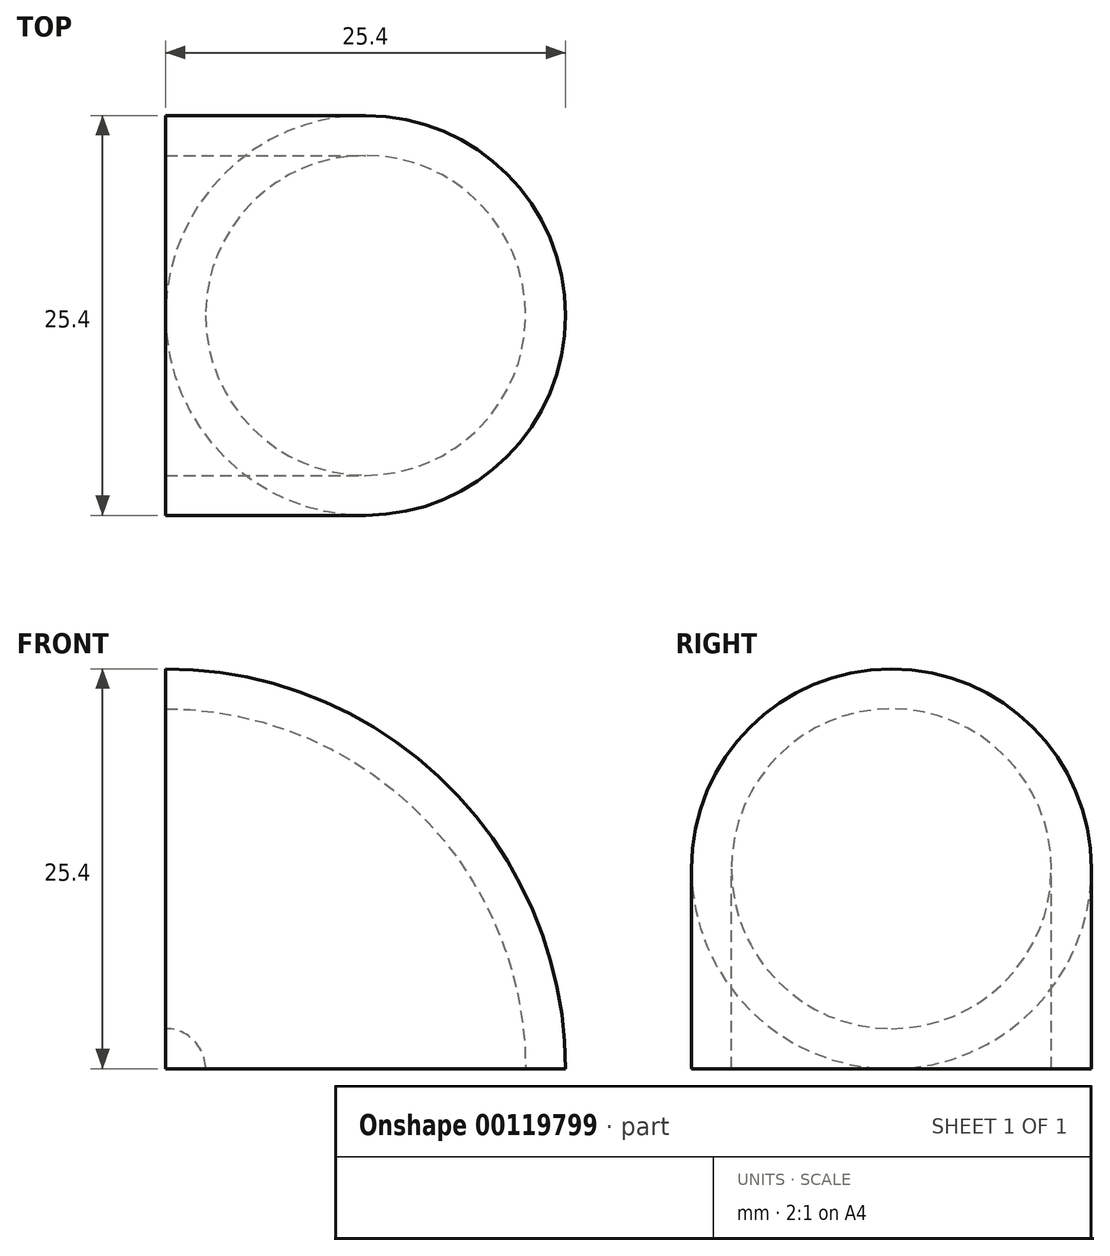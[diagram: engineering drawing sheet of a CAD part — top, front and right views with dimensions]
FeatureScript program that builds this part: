
annotation { "Feature Type Name" : "Feature", "Feature Type Description" : "" }
export const myFeature = defineFeature(function(context is Context, id is Id, definition is map)
    precondition{}
    {
        {
            var Q0;
            Q0=qCreatedBy(makeId("Right.planeOp"),FACE);
            var sketch = newSketch(context, id + "F0", { "sketchPlane" : qUnion([Q0])});
            skCircle(sketch, "E0", {"center": v(-36.71, 20.04) * mm, "radius": 12.7 * mm});
            skSolve(sketch);
        }
        {
            var Q0;
            Q0=qCreatedBy(makeId("Right.planeOp"),FACE);
            var sketch = newSketch(context, id + "F1", { "sketchPlane" : qUnion([Q0])});
            skLineSegment(sketch, "E1", {"start": v(-61.1, 7.34) * mm, "end": v(-7.29, 7.34) * mm});
            skSolve(sketch);
        }
        {
            var Q0;
            Q0=makeQuery(id+"F0.imprint","IMPRINT",FACE,{"disambiguationData":[TD([[makeQuery(id+"F0.imprint","IMPRINT",EDGE,{"derivedFrom":sQuery(id+"F0.wireOp",EDGE,"E0")}),1.0]])]});
            var Q1;
            Q1=sQuery(id+"F1.wireOp",EDGE,"E1");
            revolve(context, id + "F2", {"entities" : qUnion([Q0]), "axis" : qUnion([Q1]), "revolveType" : RevolveType.ONE_DIRECTION, "angle" : 90 * degree});
        }
        {
            var Q0;
            Q0=makeQuery(id+"F2.opRevolve","CAP_FACE",FACE,{"disambiguationData":[OSD([sQuery(id+"F0.wireOp",EDGE,"E0")])],"isStart":false});
            var Q1;
            Q1=makeQuery(id+"F2.opRevolve","CAP_FACE",FACE,{"disambiguationData":[OSD([sQuery(id+"F0.wireOp",EDGE,"E0")])],"isStart":true});
            shell(context, id + "F3", {"entities" : qUnion([Q0, Q1]), "thickness" : 2.54 * mm});
        }
    });
